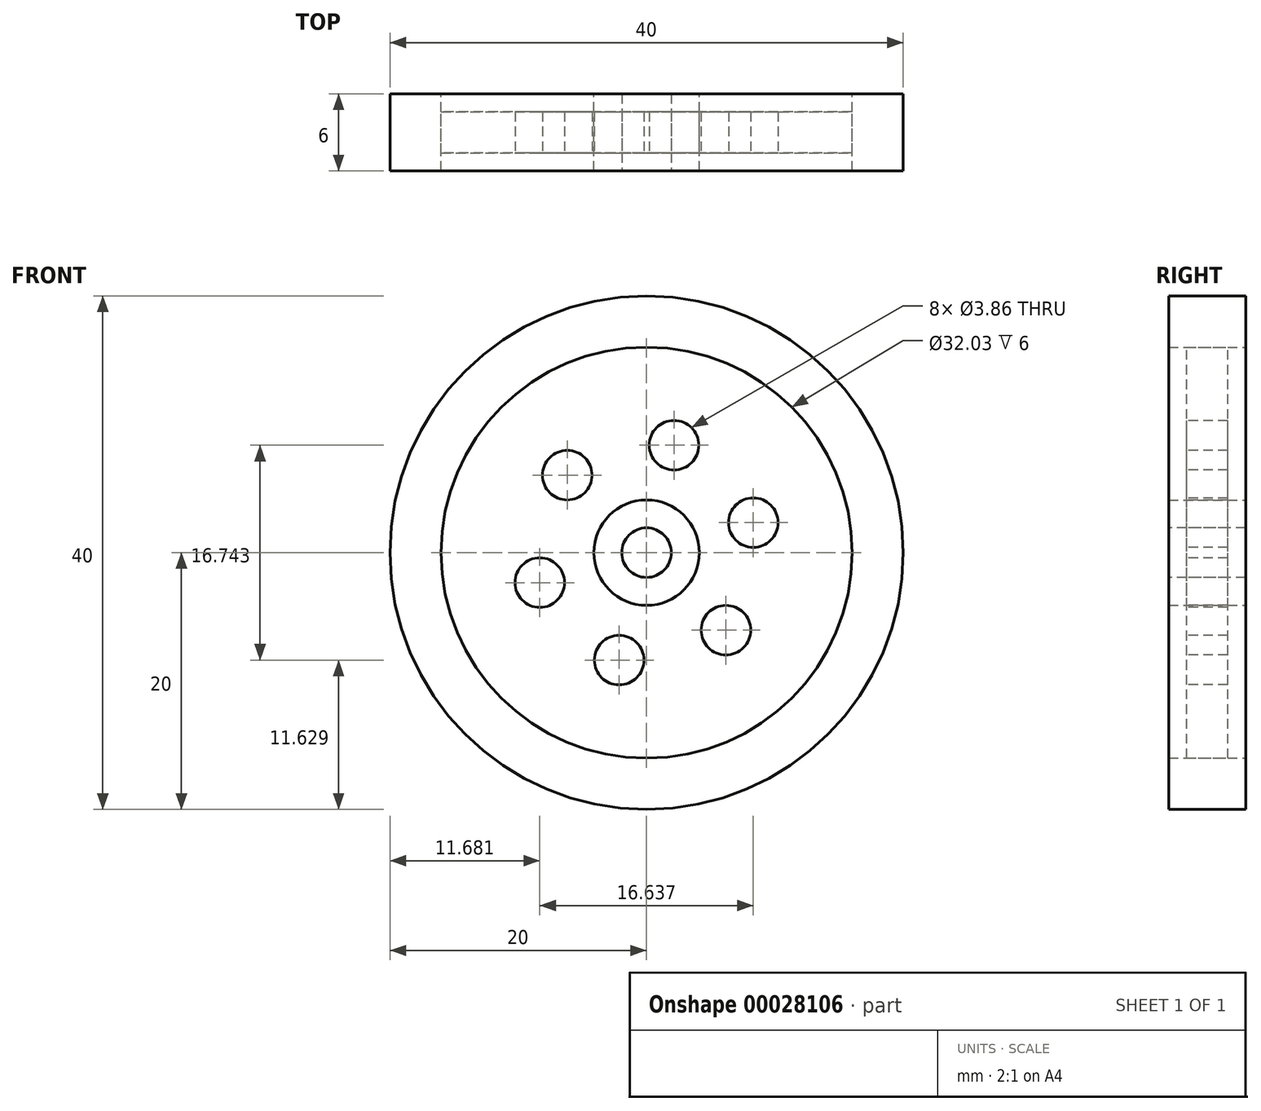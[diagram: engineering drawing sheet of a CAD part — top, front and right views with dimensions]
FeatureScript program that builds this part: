
annotation { "Feature Type Name" : "Feature", "Feature Type Description" : "" }
export const myFeature = defineFeature(function(context is Context, id is Id, definition is map)
    precondition{}
    {
        {
            var Q0;
            Q0=qCreatedBy(makeId("Front.planeOp"),FACE);
            var sketch = newSketch(context, id + "F0", { "sketchPlane" : qUnion([Q0])});
            skCircle(sketch, "E0", {"center": v(0, 0) * mm, "radius": 16.02 * mm});
            skCircle(sketch, "E1", {"center": v(0, 0) * mm, "radius": 20 * mm});
            skCircle(sketch, "E2", {"center": v(0, 0) * mm, "radius": 4.11 * mm});
            skSolve(sketch);
        }
        {
            var Q0;
            Q0=qSketchRegion(id+"F0",true);
            var Q1;
            Q1=makeQuery(id+"F0.imprint","IMPRINT",FACE,{"disambiguationData":[TD([[makeQuery(id+"F0.imprint","IMPRINT",EDGE,{"derivedFrom":sQuery(id+"F0.wireOp",EDGE,"E2")}),1.0]])]});
            extrude(context, id + "F1", {"entities" : qUnion([Q0, Q1]), "endBound" : BoundingType.SYMMETRIC, "depth" : 6 * mm});
        }
        {
            var Q0;
            Q0=qCreatedBy(makeId("Front.planeOp"),FACE);
            var sketch = newSketch(context, id + "F2", { "sketchPlane" : qUnion([Q0])});
            skCircle(sketch, "E3", {"center": v(0, 0) * mm, "radius": 16.02 * mm});
            skSolve(sketch);
        }
        {
            var Q0;
            Q0=qSketchRegion(id+"F2",true);
            extrude(context, id + "F3", {"entities" : qUnion([Q0]), "endBound" : BoundingType.SYMMETRIC, "depth" : 3.2 * mm});
        }
        {
            var Q0;
            Q0=makeQuery(id+"F1.opExtrude","CAP_FACE",FACE,{"disambiguationData":[OSD([sQuery(id+"F0.wireOp",EDGE,"E2")])],"isStart":false});
            var sketch = newSketch(context, id + "F4", { "sketchPlane" : qUnion([Q0])});
            skCircle(sketch, "E4", {"center": v(0, 0) * mm, "radius": 1.93 * mm});
            skSolve(sketch);
        }
        {
            var Q0;
            Q0=makeQuery(id+"F4.imprint","IMPRINT",FACE,{"disambiguationData":[TD([[makeQuery(id+"F4.imprint","IMPRINT",EDGE,{"derivedFrom":sQuery(id+"F4.wireOp",EDGE,"E4")}),1.0]])]});
            extrude(context, id + "F5", {"entities" : qUnion([Q0]), "operationType" : NewBodyOperationType.REMOVE, "oppositeDirection" : true, "depth" : 25 * mm});
        }
        {
            var Q0;
            Q0=makeQuery(id+"F3.opExtrude","CAP_FACE",FACE,{"disambiguationData":[OSD([sQuery(id+"F2.wireOp",EDGE,"E3")])],"isStart":false});
            var sketch = newSketch(context, id + "F6", { "sketchPlane" : qUnion([Q0])});
            skLineSegment(sketch, "E5", {"start": v(0, 0) * mm, "end": v(-10.18, -2.86) * mm});
            skCircle(sketch, "E6", {"center": v(-8.32, -2.33) * mm, "radius": 1.93 * mm});
            skLineSegment(sketch, "E7", {"start": v(0, 0) * mm, "end": v(-2.62, -10.24) * mm});
            skLineSegment(sketch, "E8", {"start": v(0, 0) * mm, "end": v(7.56, -7.39) * mm});
            skLineSegment(sketch, "E9", {"start": v(0, 0) * mm, "end": v(10.18, 2.86) * mm});
            skLineSegment(sketch, "E10", {"start": v(0, 0) * mm, "end": v(2.62, 10.24) * mm});
            skLineSegment(sketch, "E11", {"start": v(0, 0) * mm, "end": v(-7.56, 7.39) * mm});
            skCircle(sketch, "E12", {"center": v(-2.14, -8.37) * mm, "radius": 1.93 * mm});
            skCircle(sketch, "E13", {"center": v(6.18, -6.04) * mm, "radius": 1.93 * mm});
            skCircle(sketch, "E14", {"center": v(8.32, 2.33) * mm, "radius": 1.93 * mm});
            skCircle(sketch, "E15", {"center": v(2.14, 8.37) * mm, "radius": 1.93 * mm});
            skCircle(sketch, "E16", {"center": v(-6.18, 6.04) * mm, "radius": 1.93 * mm});
            skSolve(sketch);
        }
        {
            var Q0;
            Q0=qSketchRegion(id+"F6",true);
            extrude(context, id + "F7", {"entities" : qUnion([Q0]), "operationType" : NewBodyOperationType.REMOVE, "endBound" : BoundingType.THROUGH_ALL, "oppositeDirection" : true, "depth" : 25 * mm});
        }
    });
